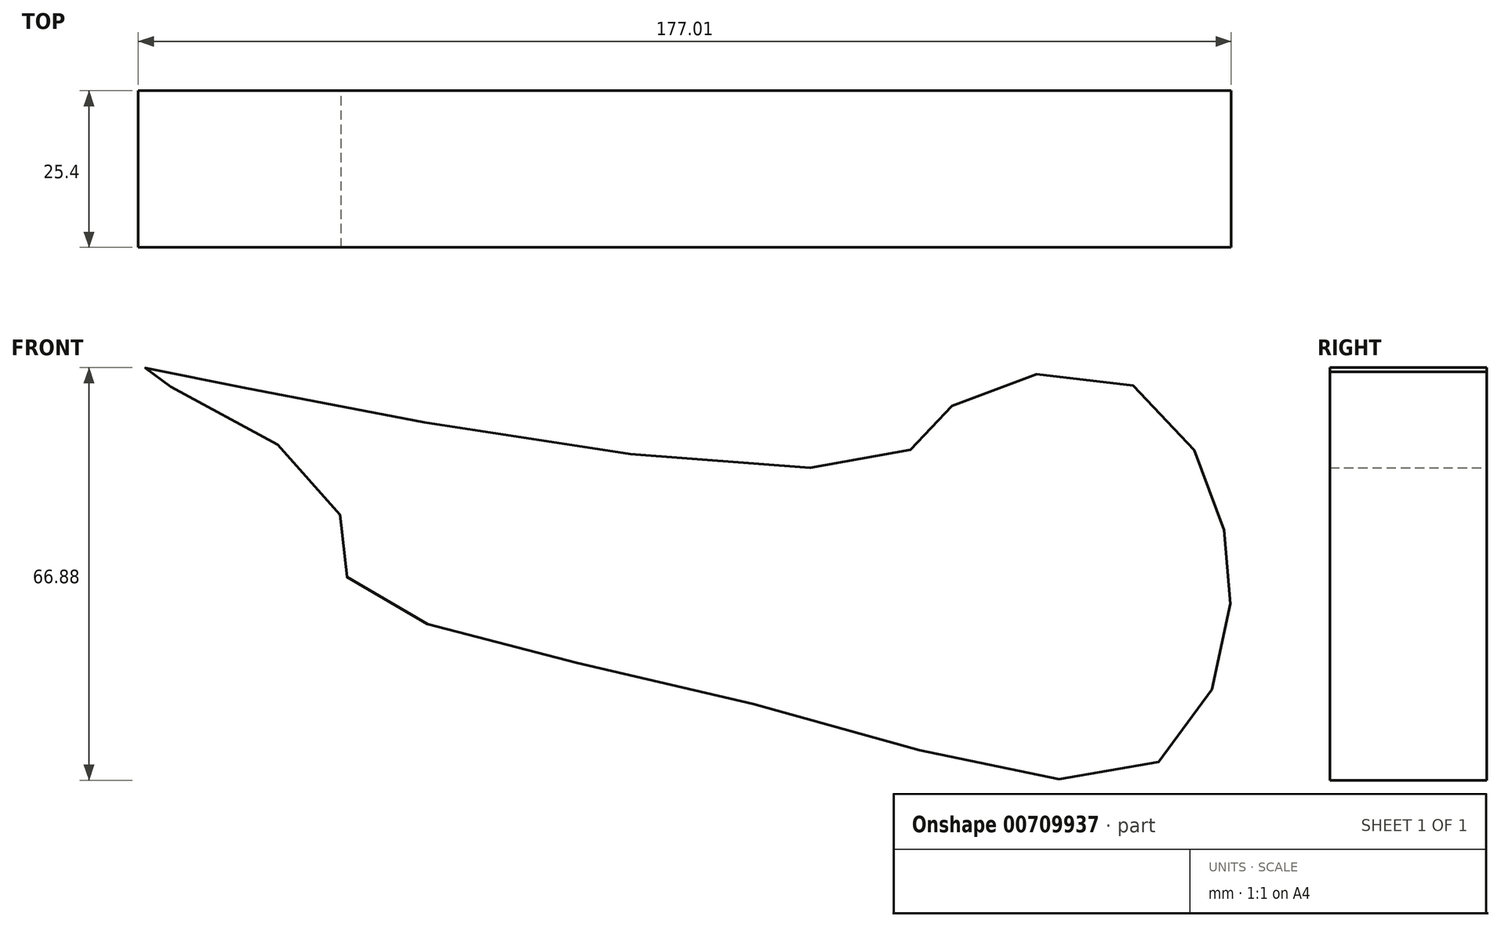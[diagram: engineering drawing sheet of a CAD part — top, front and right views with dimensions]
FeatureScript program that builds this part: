
annotation { "Feature Type Name" : "Feature", "Feature Type Description" : "" }
export const myFeature = defineFeature(function(context is Context, id is Id, definition is map)
    precondition{}
    {
        {
            var Q0;
            Q0=qCreatedBy(makeId("Front.planeOp"),FACE);
            var sketch = newSketch(context, id + "F0", { "sketchPlane" : qUnion([Q0])});
            skFitSpline(sketch, "E0", {"points": [v(-94.56, 38.63) * mm, v(9.87, 27) * mm, v(19.84, 35.58) * mm, v(47.82, 39.74) * mm, v(63.05, 19.24) * mm, v(64.71, 0) * mm, v(51.97, -22.86) * mm, v(-13.12, -12.34) * mm, v(-77.94, 7.88) * mm, v(-80.7, 22.01) * mm, v(-111.45, 41.4) * mm, v(-94.56, 38.63) * mm]});
            skSolve(sketch);
        }
        {
            var Q0;
            Q0=makeQuery(id+"F0.imprint","IMPRINT",FACE,{"disambiguationData":[TD([[makeQuery(id+"F0.imprint","IMPRINT",EDGE,{"derivedFrom":sQuery(id+"F0.wireOp",EDGE,"E0")}),-1.0]])]});
            extrude(context, id + "F1", {"entities" : qUnion([Q0]), "depth" : 12.7 * mm, "offsetDistance" : 25.4 * mm, "hasSecondDirection" : true, "secondDirectionOppositeDirection" : true, "secondDirectionDepth" : 12.7 * mm});
        }
    });
